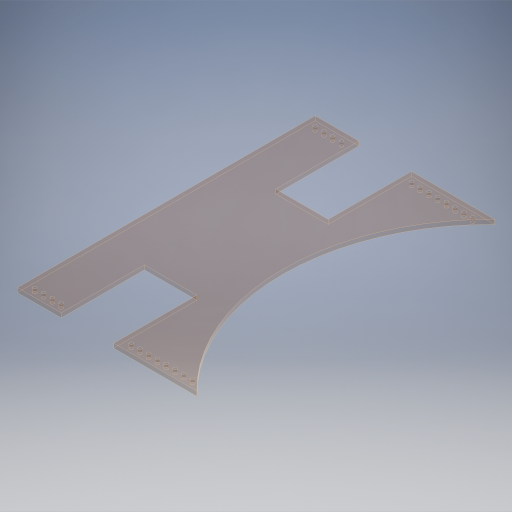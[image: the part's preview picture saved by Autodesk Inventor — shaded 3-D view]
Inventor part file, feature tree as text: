
AUTODESK INVENTOR PART (.ipt)
format: ipt  version: 2024.2 (Build 282272000, 272)  size: 333,312 bytes
history: native  units: in
note: dims shown in document units (in); Inventor stores cm internally (conversion verified against a paired STEP export)
features: extrude x1, sketch x1
ambient origin geometry x8: Origin, YZ Plane, XZ Plane, XY Plane, X Axis, Y Axis, Z Axis, Center Point
bodies: Solid1 (feature_tree)
feature tree (2):
  extrude  "Extrusion1"  Depth=17.0in
  sketch  "Sketch1"  dims[d0=23.748in d1=17.0in d2=2.5in d3=4.75in d4=3.0in d5=2.5in d6=4.75in d7=3.0in d8=4.75in d9=4.75in d10=0.196in d11=0.5in d12=0.5in d13=1.5748in d15=0.5in d16=0.3937in d18=1.0in d20=0.196in d21=0.5in d22=0.5in d23=3.1496in d25=0.5in d26=0.3937in d28=1.0in d30=0.5in d31=0.25in d32=0.0in]
